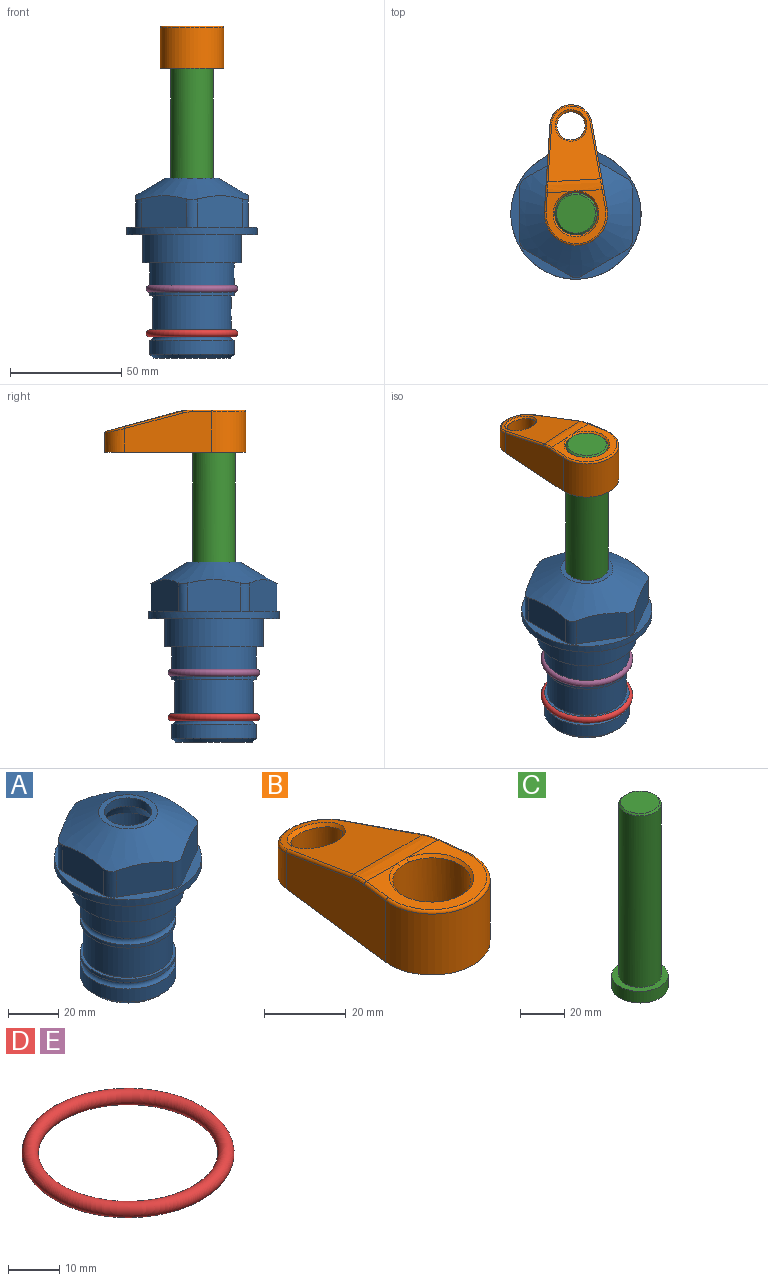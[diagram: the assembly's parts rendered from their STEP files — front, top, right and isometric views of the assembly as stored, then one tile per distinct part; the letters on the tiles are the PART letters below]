
ASSEMBLY  parts=5 mates=3
PART A: 36 faces, bbox 58.7x58.7x81 mm
  f0: cylinder r=17.78mm len=35.56mm, axis (0,0,1), area 1670.8mm2, adj f23,f24,f31
  f1: cylinder r=19.05mm len=38.1mm, axis (0,0,1), area 1191.9mm2, adj f26,f27,f30
  f2: plane 58.66x58.66mm, normal (0,0,-1), area 1150.6mm2, adj f3,f28
  f3: cylinder r=29.33mm len=58.66mm, axis (0,0,-1), area 585.1mm2, adj f2,f4
  f4: plane 58.66x58.66mm, normal (0,0,1), area 475.9mm2, adj f3,f5,f6,f7,f8,f9,f10,f11
  f5: plane 20.32x14.34mm, normal (-0.5,0.87,0), area 324.4mm2, adj f4,f15,f16,f17
  f6: plane 20.32x14.34mm, normal (0.5,0.87,0), area 324.4mm2, adj f4,f14,f15,f17
  f7: plane 23.48x14.34mm, normal (1,0,0), area 324.4mm2, adj f4,f13,f14,f17
  f8: plane 20.32x14.34mm, normal (0.5,-0.87,0), area 324.4mm2, adj f4,f12,f13,f17
  f9: plane 20.32x14.34mm, normal (-0.5,-0.87,0), area 324.4mm2, adj f4,f11,f12,f17
  f10: plane 23.48x14.34mm, normal (-1,0,0), area 324.4mm2, adj f4,f11,f16,f17
  f11: cylinder r=5.08mm len=12.85mm, axis (0,0,-1), area 67.2mm2, adj f4,f9,f10,f17
  f12: cylinder r=5.08mm len=12.85mm, axis (0,0,-1), area 67.2mm2, adj f4,f8,f9,f17
  f13: cylinder r=5.08mm len=12.85mm, axis (0,0,-1), area 67.2mm2, adj f4,f7,f8,f17
  f14: cylinder r=5.08mm len=12.85mm, axis (0,0,-1), area 67.2mm2, adj f4,f6,f7,f17
  f15: cylinder r=5.08mm len=12.85mm, axis (0,0,-1), area 67.2mm2, adj f4,f5,f6,f17
  f16: cylinder r=5.08mm len=12.85mm, axis (0,0,-1), area 67.2mm2, adj f4,f5,f10,f17
  f17: cone r=11.73mm half-angle=60deg, axis (0,0,-1), area 2071.8mm2, adj f5,f6,f7,f8,f9,f10,f11,f12
  f18: plane 23.46x23.46mm, normal (0,0,1), area 147.4mm2, adj f17,f35
  f19: plane 34.93x34.93mm, normal (0,0,-1), area 958mm2, adj f29
  f20: cylinder r=19.05mm len=38.1mm, axis (0,0,1), area 760.1mm2, adj f21,f29
  f21: torus R=19.05mm, axis (0,0,1), area 565.3mm2, adj f20,f22
  f22: cylinder r=19.05mm len=38.1mm, axis (0,0,1), area 190mm2, adj f21,f23
  f23: plane 38.1x38.1mm, normal (0,0,1), area 146.9mm2, adj f0,f22
  f24: plane 38.1x38.1mm, normal (0,0,-1), area 146.9mm2, adj f0,f25
  f25: cylinder r=19.05mm len=38.1mm, axis (0,0,1), area 190mm2, adj f24,f26
  f26: torus R=19.05mm, axis (0,0,1), area 565.3mm2, adj f1,f25
  f27: plane 44.45x44.45mm, normal (0,0,-1), area 411.7mm2, adj f1,f28
  f28: cylinder r=22.23mm len=44.45mm, axis (0,0,1), area 1773.5mm2, adj f2,f27
  f29: cone r=19.05mm half-angle=45deg, axis (0,0,1), area 257.5mm2, adj f19,f20
  f30: cylinder r=3.17mm len=6.75mm, axis (-1,0,0), area 128mm2, adj f1,f33
  f31: cylinder r=3.17mm len=6.35mm, axis (-1,0,0), area 102.5mm2, adj f0,f33
  f32: plane 25.4x25.4mm, normal (0,0,1), area 506.7mm2, adj f33
  f33: cylinder r=12.7mm len=66.42mm, axis (0,0,-1), area 5236.2mm2, adj f30,f31,f32,f34
  f34: cone r=9.53mm half-angle=30deg, axis (0,0,-1), area 443.4mm2, adj f33,f35
  f35: cylinder r=9.53mm len=19.05mm, axis (0,0,-1), area 240.9mm2, adj f18,f34
PART B: 31 faces, bbox 31.7x65.5x19.8 mm
  f0: plane 39.12x18.26mm, normal (0.99,0.12,0), area 612.2mm2, adj f1,f4,f7,f11,f13,f15
  f1: cylinder r=9.53mm len=18.91mm, axis (0,0,-1), area 296.1mm2, adj f0,f2,f7,f17
  f2: plane 39.12x18.26mm, normal (-0.99,0.12,0), area 612.2mm2, adj f1,f4,f7,f12,f14,f16
  f3: cylinder r=6.35mm len=12.7mm, axis (0,0,-1), area 362.4mm2, adj f7,f18
  f4: cylinder r=14.29mm len=28.58mm, axis (0,0,-1), area 882.2mm2, adj f0,f2,f7,f10
  f5: cylinder r=9.53mm len=19.05mm, axis (0,0,-1), area 1092.6mm2, adj f7,f19,f20
  f6: plane 26.99x23.69mm, normal (0,0,1), area 216.2mm2, adj f9,f10,f11,f12,f19
  f7: plane 63.5x28.58mm, normal (0,0,-1), area 661.8mm2, adj f0,f1,f2,f3,f4,f5,f22,f23
  f8: plane 33.52x23.6mm, normal (0,0.26,0.97), area 486mm2, adj f9,f15,f16,f17,f18
  f9: cylinder r=19.05mm len=24.72mm, axis (1,0,0), area 120.4mm2, adj f6,f8,f13,f14,f20
  f10: torus R=13.49mm, axis (0,0,1), area 59mm2, adj f4,f6,f11,f12
  f11: cylinder r=0.79mm len=8.67mm, axis (0.12,-0.99,0), area 10.8mm2, adj f0,f6,f10,f13
  f12: cylinder r=0.79mm len=8.67mm, axis (0.12,0.99,0), area 10.8mm2, adj f2,f6,f10,f14
  f13: bspline ~4.95x1.42mm, area 6.1mm2, adj f0,f9,f11,f15
  f14: bspline ~4.95x1.42mm, area 6.1mm2, adj f2,f9,f12,f16
  f15: cylinder r=0.79mm len=25.95mm, axis (0.12,-0.96,0.26), area 32.9mm2, adj f0,f8,f13,f17
  f16: cylinder r=0.79mm len=25.95mm, axis (0.12,0.96,-0.26), area 32.9mm2, adj f2,f8,f14,f17
  f17: bspline ~18.91x8.38mm, area 30mm2, adj f1,f8,f15,f16
  f18: bspline ~14.29x14.29mm, area 48.3mm2, adj f3,f8
  f19: cone r=9.53mm half-angle=45deg, axis (0,0,1), area 66.5mm2, adj f5,f6,f20
  f20: bspline ~3.22x0.96mm, area 3.5mm2, adj f5,f9,f19
  f21: plane 2.75x2.72mm, normal (0,0,-1), area 2.9mm2, adj f23,f25,f28
  f22: plane 23.05x15.88mm, normal (-0.99,-0.12,0), area 323.6mm2, adj f7,f25,f26,f27,f28,f29
  f23: plane 23.05x15.88mm, normal (0.99,-0.12,0), area 323.6mm2, adj f7,f21,f25,f27,f28,f30
  f24: cylinder r=9.53mm len=10.69mm, axis (0,0,-1), area 114.7mm2, adj f7,f27,f29,f30
  f25: cylinder r=12.7mm len=20.59mm, axis (0,0,-1), area 381.1mm2, adj f7,f21,f22,f23,f26,f28
  f26: plane 2.75x2.72mm, normal (0,0,-1), area 2.9mm2, adj f22,f25,f28
  f27: plane 19.72x18.37mm, normal (0,-0.26,-0.97), area 291.8mm2, adj f22,f23,f24,f28,f29,f30
  f28: cylinder r=15.88mm len=19.92mm, axis (1,0,0), area 54.8mm2, adj f21,f22,f23,f25,f26,f27
  f29: cylinder r=1.59mm len=11mm, axis (0,0,-1), area 34.7mm2, adj f7,f22,f24,f27
  f30: cylinder r=1.59mm len=11mm, axis (0,0,-1), area 34.7mm2, adj f7,f23,f24,f27
PART C: 6 faces, bbox 25.4x25.4x101.6 mm
  f0: plane 17.46x17.46mm, normal (0,0,1), area 239.5mm2, adj f5
  f1: plane 25.4x25.4mm, normal (0,0,-1), area 506.7mm2, adj f2
  f2: cylinder r=12.7mm len=25.4mm, axis (0,0,1), area 506.7mm2, adj f1,f3
  f3: plane 25.4x25.4mm, normal (0,0,1), area 221.7mm2, adj f2,f4
  f4: cylinder r=9.53mm len=94.46mm, axis (0,0,1), area 5653mm2, adj f3,f5
  f5: cone r=8.73mm half-angle=45deg, axis (0,0,-1), area 64.4mm2, adj f0,f4
PART D: 1 faces, bbox 44.7x44.7x3.2 mm
  f0: torus R=19.05mm, axis (0,0,1), area 1193.9mm2
PART E: same geometry as D
PLACE A at identity fixed
PLACE B rot(axis=(0,0,1),3.2deg) t=(0,0,30.41)mm
PLACE C rot(axis=(0,0,1),3.2deg) t=(0,0,30.41)mm
PLACE D t=(0,0,-20)mm
PLACE E at identity
MATE fastened D.f0 <-> A.f0  axis (0,0,1) through (0,0,-44.51)mm
MATE cylindrical C.f2 <-> A.f0  axis (0,0,-1) through (0,0,-7.69)mm
MATE fastened C.f2 <-> B.f4  axis (0,0,1) through (0,0,93.91)mm
